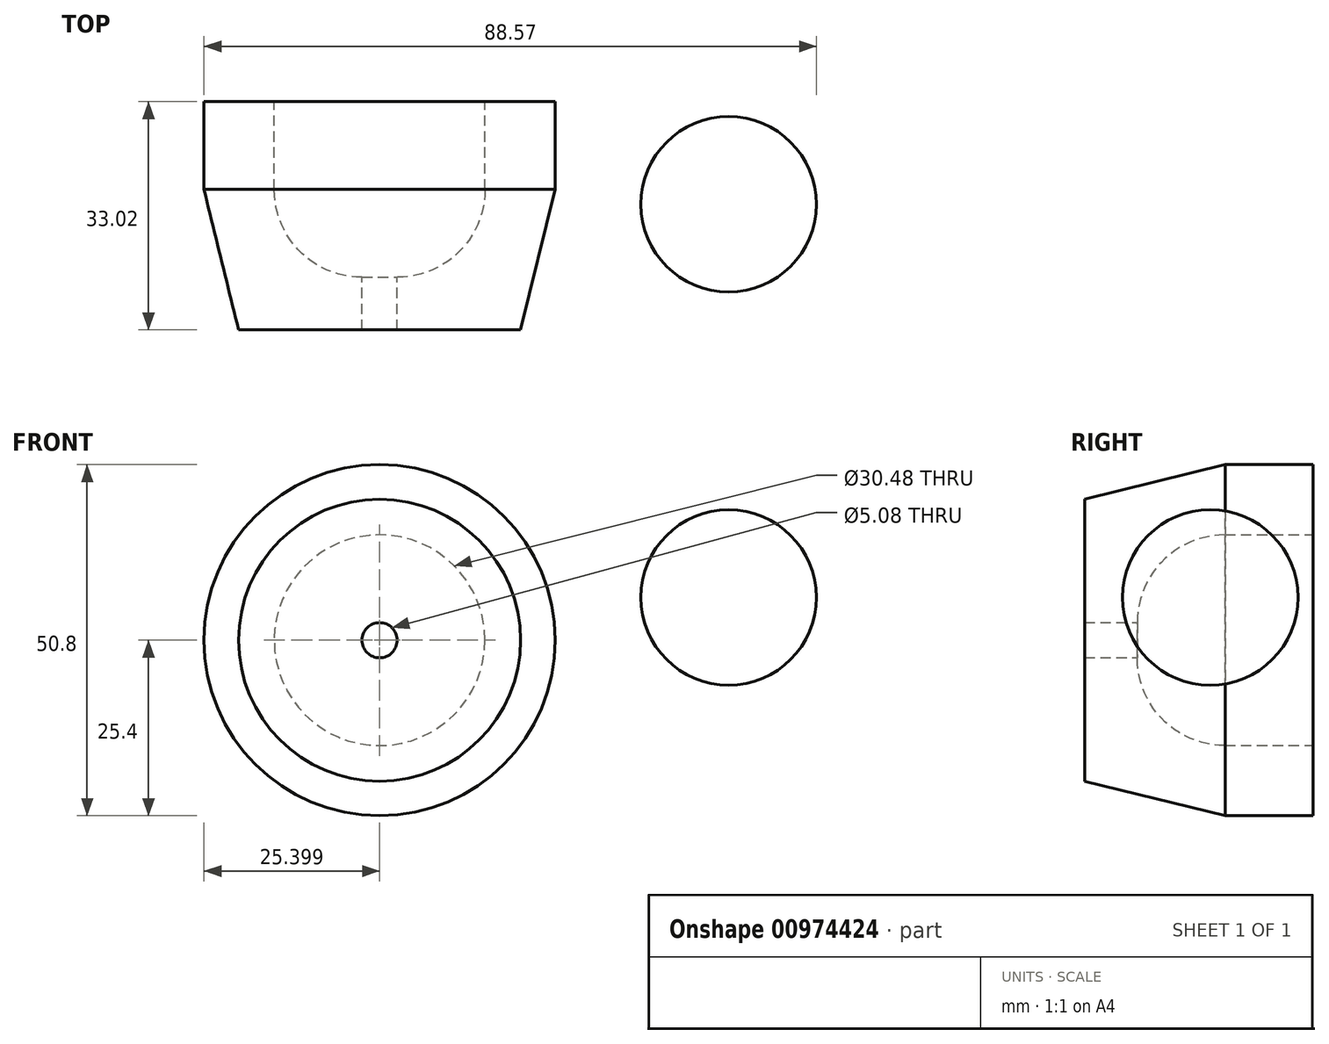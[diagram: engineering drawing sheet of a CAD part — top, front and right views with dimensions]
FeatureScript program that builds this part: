
annotation { "Feature Type Name" : "Feature", "Feature Type Description" : "" }
export const myFeature = defineFeature(function(context is Context, id is Id, definition is map)
    precondition{}
    {
        {
            var Q0;
            Q0=qCreatedBy(makeId("Top.planeOp"),FACE);
            var sketch = newSketch(context, id + "F0", { "sketchPlane" : qUnion([Q0])});
            skLineSegment(sketch, "E0", {"start": v(-20.4, 37.33) * mm, "end": v(-20.4, -30.29) * mm, "construction": true});
            skLineSegment(sketch, "E1", {"start": v(0, -18.17) * mm, "end": v(5, 2.15) * mm});
            skLineSegment(sketch, "E2", {"start": v(5, 2.15) * mm, "end": v(-5.15, 2.15) * mm});
            skArc(sketch, "E3", {"start": v(-17.85, -10.55) * mm, "mid": v(-8.87, -6.83) * mm, "end": v(-5.15, 2.15) * mm});
            skLineSegment(sketch, "E4", {"start": v(-17.85, -10.55) * mm, "end": v(-17.85, -18.17) * mm});
            skLineSegment(sketch, "E5", {"start": v(-17.85, -18.17) * mm, "end": v(0, -18.17) * mm});
            skLineSegment(sketch, "E6", {"start": v(-5.15, 2.15) * mm, "end": v(-5.15, 14.85) * mm});
            skLineSegment(sketch, "E7", {"start": v(-5.15, 14.85) * mm, "end": v(5, 14.85) * mm});
            skLineSegment(sketch, "E8", {"start": v(5, 2.15) * mm, "end": v(5, 14.85) * mm});
            skSolve(sketch);
        }
        {
            var Q0;
            Q0=makeQuery(id+"F0.imprint","IMPRINT",FACE,{"disambiguationData":[TD([[makeQuery(id+"F0.imprint","IMPRINT",EDGE,{"derivedFrom":sQuery(id+"F0.wireOp",EDGE,"E2")}),-1.0]])]});
            var Q1;
            Q1=makeQuery(id+"F0.imprint","IMPRINT",FACE,{"disambiguationData":[TD([[makeQuery(id+"F0.imprint","IMPRINT",EDGE,{"derivedFrom":sQuery(id+"F0.wireOp",EDGE,"E1")}),1.0]])]});
            var Q2;
            Q2=sQuery(id+"F0.wireOp",EDGE,"E0");
            revolve(context, id + "F1", {"surfaceOperationType" : NewSurfaceOperationType.NEW, "entities" : qUnion([Q0, Q1]), "axis" : qUnion([Q2]), "revolveType" : RevolveType.FULL});
        }
        {
            var Q0;
            Q0=qCreatedBy(makeId("Front.planeOp"),FACE);
            var sketch = newSketch(context, id + "F2", { "sketchPlane" : qUnion([Q0])});
            skLineSegment(sketch, "E9", {"start": v(42.78, 6.19) * mm, "end": v(17.38, 6.19) * mm});
            skArc(sketch, "E10", {"start": v(17.38, 6.19) * mm, "mid": v(30.08, -6.51) * mm, "end": v(42.78, 6.19) * mm});
            skLineSegment(sketch, "E11", {"start": v(47.87, 6.19) * mm, "end": v(11.97, 6.19) * mm, "construction": true});
            skSolve(sketch);
        }
        {
            var Q0;
            Q0=makeQuery(id+"F2.imprint","IMPRINT",FACE,{"disambiguationData":[TD([[makeQuery(id+"F2.imprint","IMPRINT",EDGE,{"derivedFrom":sQuery(id+"F2.wireOp",EDGE,"E9")}),1.0]])]});
            var Q1;
            Q1=sQuery(id+"F2.wireOp",EDGE,"E11");
            revolve(context, id + "F3", {"surfaceOperationType" : NewSurfaceOperationType.NEW, "entities" : qUnion([Q0]), "axis" : qUnion([Q1]), "revolveType" : RevolveType.FULL});
        }
    });
